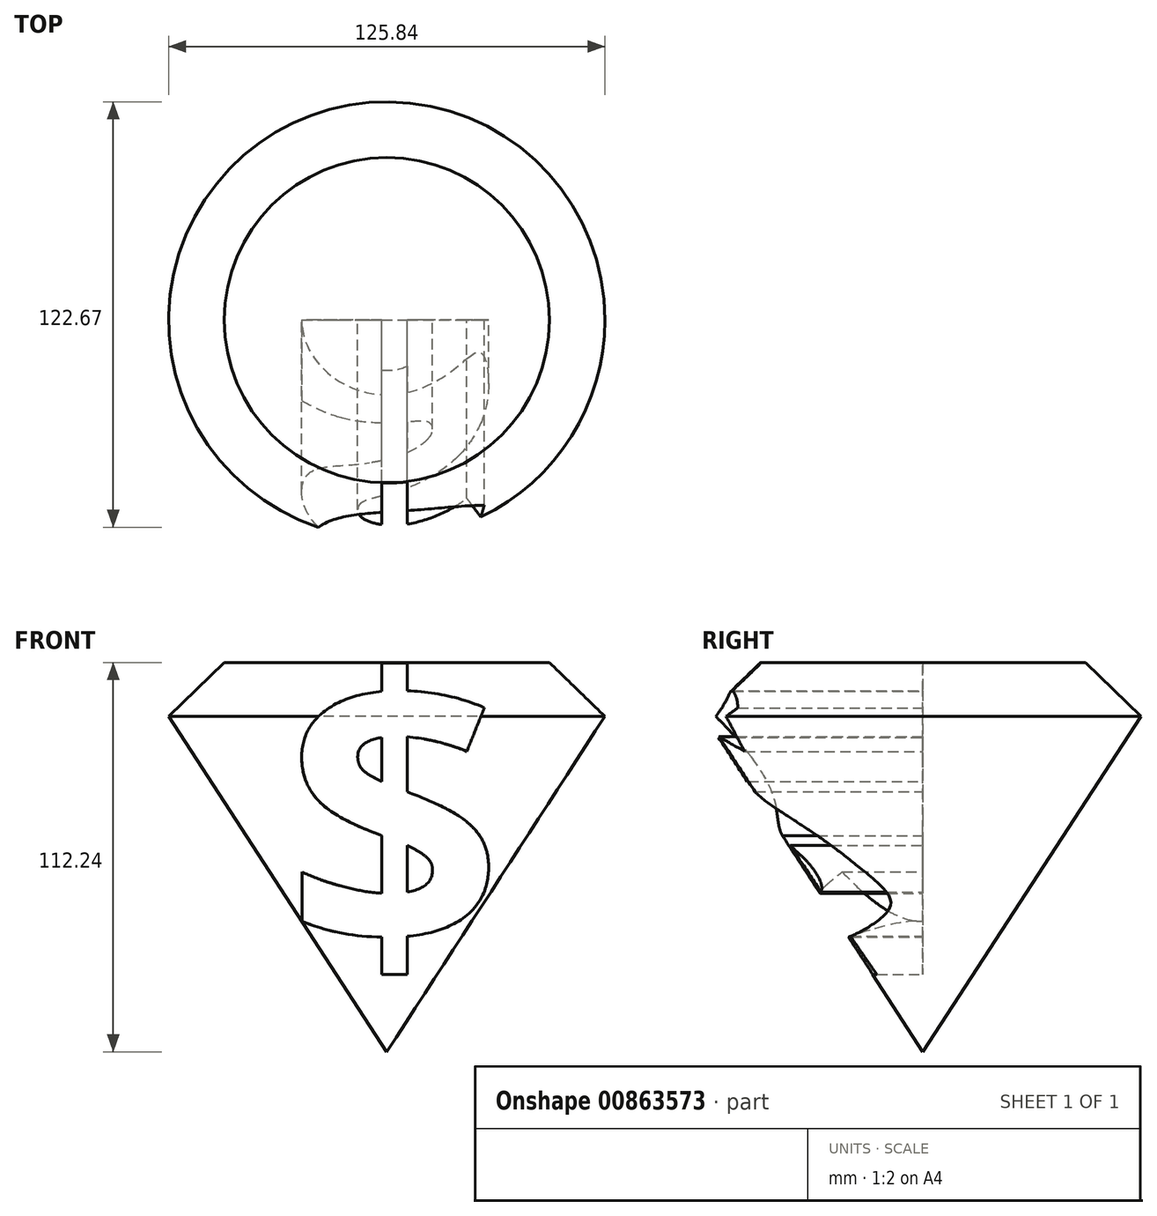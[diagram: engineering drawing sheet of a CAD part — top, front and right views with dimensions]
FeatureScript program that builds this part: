
annotation { "Feature Type Name" : "Feature", "Feature Type Description" : "" }
export const myFeature = defineFeature(function(context is Context, id is Id, definition is map)
    precondition{}
    {
        {
            var Q0;
            Q0=qCreatedBy(makeId("Front.planeOp"),FACE);
            var sketch = newSketch(context, id + "F0", { "sketchPlane" : qUnion([Q0])});
            skLineSegment(sketch, "E0", {"start": v(-46.89, 55.96) * mm, "end": v(-62.92, 40.4) * mm});
            skLineSegment(sketch, "E1", {"start": v(-62.92, 40.4) * mm, "end": v(0, -56.28) * mm});
            skPoint(sketch, "E2.end.orphan", {"position": v(74.92, 40.4) * mm});
            skLineSegment(sketch, "E3", {"start": v(-46.89, 55.96) * mm, "end": v(0, 55.96) * mm});
            skLineSegment(sketch, "E4", {"start": v(0, 55.96) * mm, "end": v(0, -56.28) * mm});
            skSolve(sketch);
        }
        {
            var Q0;
            Q0 = qSketchRegion(id + "F0", true);
            var Q1;
            Q1=sQuery(id+"F0.wireOp",EDGE,"E4");
            revolve(context, id + "F1", {"surfaceOperationType" : NewSurfaceOperationType.NEW, "entities" : qUnion([Q0]), "axis" : qUnion([Q1]), "revolveType" : RevolveType.FULL});
        }
        {
            var Q0;
            Q0=qCreatedBy(makeId("Front.planeOp"),FACE);
            var sketch = newSketch(context, id + "F2", { "sketchPlane" : qUnion([Q0])});
            skText(sketch, "E5", { "text": "$", "fontName": "OpenSans-Bold.ttf"});
            const initialGuessF2  = {"E5": [-0.02929, -0.02761, 1, 0, 0.0792]};
            skSetInitialGuess(sketch, initialGuessF2);
            skSolve(sketch);
        }
        {
            var Q0;
            Q0 = qSketchRegion(id + "F2", true);
            extrude(context, id + "F3", {"entities" : qUnion([Q0]), "operationType" : NewBodyOperationType.REMOVE, "depth" : 86.61 * mm, "offsetDistance" : 25.4 * mm});
        }
    });
